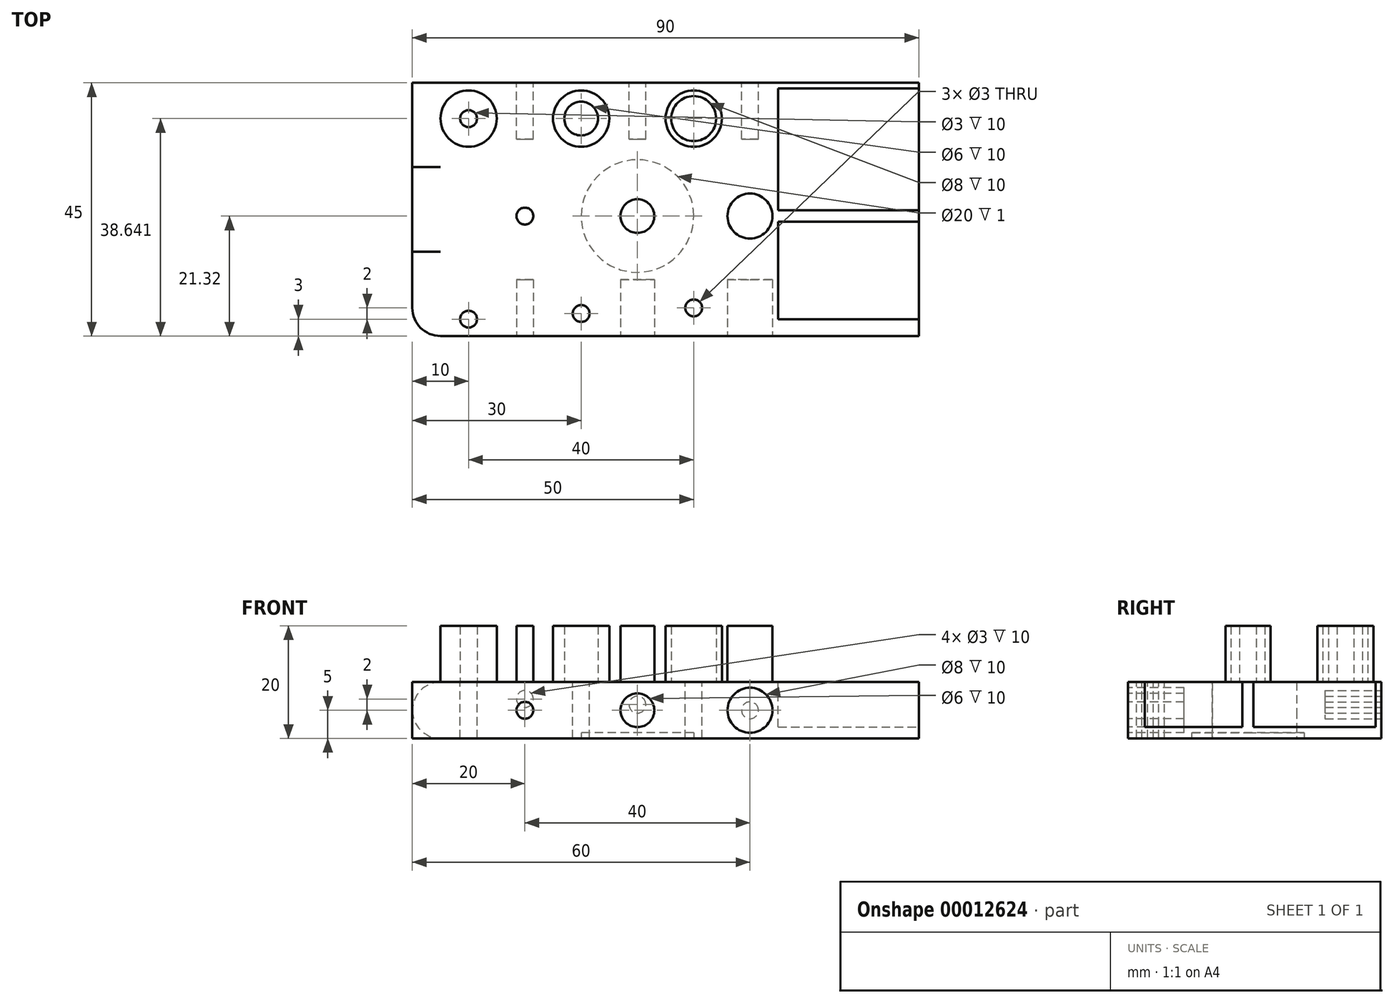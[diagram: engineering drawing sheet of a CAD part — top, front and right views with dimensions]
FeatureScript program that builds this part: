
annotation { "Feature Type Name" : "Feature", "Feature Type Description" : "" }
export const myFeature = defineFeature(function(context is Context, id is Id, definition is map)
    precondition{}
    {
        {
            var Q0;
            Q0=qCreatedBy(makeId("Top.planeOp"),FACE);
            var sketch = newSketch(context, id + "F0", { "sketchPlane" : qUnion([Q0])});
            skCircle(sketch, "E0", {"center": v(-20, 0) * mm, "radius": 1.5 * mm});
            skCircle(sketch, "E1", {"center": v(0, 0) * mm, "radius": 3 * mm});
            skCircle(sketch, "E2", {"center": v(20, 0) * mm, "radius": 4 * mm});
            skCircle(sketch, "E3", {"center": v(-10, 17.32) * mm, "radius": 5 * mm});
            skCircle(sketch, "E4", {"center": v(-30, 17.32) * mm, "radius": 5 * mm});
            skCircle(sketch, "E5", {"center": v(10, 17.32) * mm, "radius": 5 * mm});
            skCircle(sketch, "E6", {"center": v(-30, 17.32) * mm, "radius": 1.5 * mm});
            skCircle(sketch, "E7", {"center": v(-10, 17.32) * mm, "radius": 3 * mm});
            skCircle(sketch, "E8", {"center": v(10, 17.32) * mm, "radius": 4 * mm});
            skCircle(sketch, "E9", {"center": v(-30, -18.32) * mm, "radius": 1.5 * mm});
            skCircle(sketch, "E10", {"center": v(-10, -17.32) * mm, "radius": 1.5 * mm});
            skCircle(sketch, "E11", {"center": v(10, -16.32) * mm, "radius": 1.5 * mm});
            skLineSegment(sketch, "E12.bottom", {"start": v(-40, 23.68) * mm, "end": v(25, 23.68) * mm});
            skLineSegment(sketch, "E12.top", {"start": v(-40, -21.32) * mm, "end": v(25, -21.32) * mm});
            skLineSegment(sketch, "E12.left", {"start": v(-40, 23.68) * mm, "end": v(-40, -21.32) * mm});
            skLineSegment(sketch, "E12.right", {"start": v(25, 23.68) * mm, "end": v(25, -21.32) * mm});
            skLineSegment(sketch, "E13", {"start": v(-20, 0) * mm, "end": v(0, 0) * mm, "construction": true});
            skLineSegment(sketch, "E14", {"start": v(0, 0) * mm, "end": v(20, 0) * mm, "construction": true});
            skLineSegment(sketch, "E15", {"start": v(-30, 17.32) * mm, "end": v(-10, 17.32) * mm, "construction": true});
            skLineSegment(sketch, "E16", {"start": v(-10, 17.32) * mm, "end": v(10, 17.32) * mm, "construction": true});
            skLineSegment(sketch, "E17", {"start": v(0, 0) * mm, "end": v(10, 17.32) * mm, "construction": true});
            skLineSegment(sketch, "E18", {"start": v(20, 0) * mm, "end": v(10, 17.32) * mm, "construction": true});
            skLineSegment(sketch, "E19", {"start": v(-20, 0) * mm, "end": v(-10, -17.32) * mm, "construction": true});
            skLineSegment(sketch, "E20", {"start": v(0, 0) * mm, "end": v(-10, -17.32) * mm, "construction": true});
            skLineSegment(sketch, "E21.bottom", {"start": v(25, 23.68) * mm, "end": v(50, 23.68) * mm});
            skLineSegment(sketch, "E21.top", {"start": v(25, -21.32) * mm, "end": v(50, -21.32) * mm});
            skLineSegment(sketch, "E21.right", {"start": v(50, 23.68) * mm, "end": v(50, -21.32) * mm});
            skLineSegment(sketch, "E22.top", {"start": v(25, 22.68) * mm, "end": v(50, 22.68) * mm});
            skLineSegment(sketch, "E22.left", {"start": v(25, 23.68) * mm, "end": v(25, 22.68) * mm});
            skLineSegment(sketch, "E22.right", {"start": v(50, 23.68) * mm, "end": v(50, 22.68) * mm});
            skLineSegment(sketch, "E23.bottom", {"start": v(25, 1) * mm, "end": v(50, 1) * mm});
            skLineSegment(sketch, "E23.top", {"start": v(25, -1) * mm, "end": v(50, -1) * mm});
            skLineSegment(sketch, "E23.left", {"start": v(25, 1) * mm, "end": v(25, -1) * mm});
            skLineSegment(sketch, "E23.right", {"start": v(50, 1) * mm, "end": v(50, -1) * mm});
            skLineSegment(sketch, "E24.top", {"start": v(25, -18.32) * mm, "end": v(50, -18.32) * mm});
            skLineSegment(sketch, "E24.left", {"start": v(25, -21.32) * mm, "end": v(25, -18.32) * mm});
            skLineSegment(sketch, "E24.right", {"start": v(50, -21.32) * mm, "end": v(50, -18.32) * mm});
            skPoint(sketch, "E25", {"position": v(50, 0) * mm});
            skSolve(sketch);
        }
        {
            var Q0;
            Q0=qCreatedBy(makeId("Top.planeOp"),FACE);
            var sketch = newSketch(context, id + "F1", { "sketchPlane" : qUnion([Q0])});
            skLineSegment(sketch, "E26.0", {"start": v(-40, 23.68) * mm, "end": v(25, 23.68) * mm});
            skLineSegment(sketch, "E26.1", {"start": v(25, 23.68) * mm, "end": v(50, 23.68) * mm});
            skLineSegment(sketch, "E26.2", {"start": v(50, 23.68) * mm, "end": v(50, -21.32) * mm});
            skLineSegment(sketch, "E26.3", {"start": v(25, -21.32) * mm, "end": v(50, -21.32) * mm});
            skLineSegment(sketch, "E26.4", {"start": v(-40, -21.32) * mm, "end": v(25, -21.32) * mm});
            skLineSegment(sketch, "E26.5", {"start": v(-40, 23.68) * mm, "end": v(-40, -21.32) * mm});
            skSolve(sketch);
        }
        {
            var Q0;
            Q0 = qSketchRegion(id + "F1", true);
            extrude(context, id + "F2", {"entities" : qUnion([Q0]), "depth" : 10 * mm});
        }
        {
            var Q0;
            Q0=makeQuery(id+"F2.opExtrude","CAP_FACE",FACE,{"disambiguationData":[OSD([sQuery(id+"F1.wireOp",EDGE,"E26.0"),sQuery(id+"F1.wireOp",EDGE,"E26.1"),sQuery(id+"F1.wireOp",EDGE,"E26.2"),sQuery(id+"F1.wireOp",EDGE,"E26.3"),sQuery(id+"F1.wireOp",EDGE,"E26.4"),sQuery(id+"F1.wireOp",EDGE,"E26.5")])],"isStart":false});
            var sketch = newSketch(context, id + "F3", { "sketchPlane" : qUnion([Q0])});
            skCircle(sketch, "E27.0", {"center": v(-30, 17.32) * mm, "radius": 1.5 * mm});
            skCircle(sketch, "E27.1", {"center": v(-30, 17.32) * mm, "radius": 5 * mm});
            skCircle(sketch, "E27.2", {"center": v(-10, 17.32) * mm, "radius": 3 * mm});
            skCircle(sketch, "E27.3", {"center": v(-10, 17.32) * mm, "radius": 5 * mm});
            skCircle(sketch, "E27.4", {"center": v(10, 17.32) * mm, "radius": 4 * mm});
            skCircle(sketch, "E27.5", {"center": v(10, 17.32) * mm, "radius": 5 * mm});
            skCircle(sketch, "E27.6", {"center": v(20, 0) * mm, "radius": 4 * mm});
            skCircle(sketch, "E27.7", {"center": v(0, 0) * mm, "radius": 3 * mm});
            skCircle(sketch, "E27.8", {"center": v(-20, 0) * mm, "radius": 1.5 * mm});
            skSolve(sketch);
        }
        {
            var Q0;
            Q0 = qSketchRegion(id + "F3", true);
            extrude(context, id + "F4", {"entities" : qUnion([Q0]), "operationType" : NewBodyOperationType.ADD, "depth" : 10 * mm});
        }
        {
            var Q0;
            {var subQ0=sQuery(id+"F1.wireOp",EDGE,"E26.0");var subQ1=sQuery(id+"F1.wireOp",EDGE,"E26.1");var subQ2=sQuery(id+"F1.wireOp",EDGE,"E26.2");var subQ3=sQuery(id+"F1.wireOp",EDGE,"E26.3");var subQ4=sQuery(id+"F1.wireOp",EDGE,"E26.4");var subQ5=sQuery(id+"F1.wireOp",EDGE,"E26.5");Q0=makeQuery(id+"F4.boolean.opBoolean","SPLIT",FACE,{"disambiguationData":[TD([makeQuery(id+"F2.opExtrude","SWEPT_FACE",FACE,{"disambiguationData":[OSD([subQ2])]})])],"derivedFrom":makeQuery(id+"F2.opExtrude","CAP_FACE",FACE,{"disambiguationData":[OSD([subQ0,subQ1,subQ2,subQ3,subQ4,subQ5])],"isStart":false})});}
            var sketch = newSketch(context, id + "F5", { "sketchPlane" : qUnion([Q0])});
            skCircle(sketch, "E28.0", {"center": v(-30, -18.32) * mm, "radius": 1.5 * mm});
            skCircle(sketch, "E28.1", {"center": v(-10, -17.32) * mm, "radius": 1.5 * mm});
            skCircle(sketch, "E28.2", {"center": v(10, -16.32) * mm, "radius": 1.5 * mm});
            skSolve(sketch);
        }
        {
            var Q0;
            Q0 = qSketchRegion(id + "F5", true);
            extrude(context, id + "F6", {"entities" : qUnion([Q0]), "operationType" : NewBodyOperationType.REMOVE, "endBound" : BoundingType.THROUGH_ALL, "oppositeDirection" : true, "depth" : 25 * mm});
        }
        {
            var Q0;
            {var subQ0=sQuery(id+"F1.wireOp",EDGE,"E26.0");var subQ1=sQuery(id+"F1.wireOp",EDGE,"E26.1");var subQ2=sQuery(id+"F1.wireOp",EDGE,"E26.2");var subQ3=sQuery(id+"F1.wireOp",EDGE,"E26.3");var subQ4=sQuery(id+"F1.wireOp",EDGE,"E26.4");var subQ5=sQuery(id+"F1.wireOp",EDGE,"E26.5");Q0=makeQuery(id+"F4.boolean.opBoolean","SPLIT",FACE,{"disambiguationData":[TD([makeQuery(id+"F2.opExtrude","SWEPT_FACE",FACE,{"disambiguationData":[OSD([subQ2])]})])],"derivedFrom":makeQuery(id+"F2.opExtrude","CAP_FACE",FACE,{"disambiguationData":[OSD([subQ0,subQ1,subQ2,subQ3,subQ4,subQ5])],"isStart":false})});}
            var sketch = newSketch(context, id + "F7", { "sketchPlane" : qUnion([Q0])});
            skLineSegment(sketch, "E29.bottom", {"start": v(25, 22.68) * mm, "end": v(50, 22.68) * mm});
            skLineSegment(sketch, "E29.top", {"start": v(25, 1) * mm, "end": v(50, 1) * mm});
            skLineSegment(sketch, "E29.left", {"start": v(25, 22.68) * mm, "end": v(25, 1) * mm});
            skLineSegment(sketch, "E29.right", {"start": v(50, 22.68) * mm, "end": v(50, 1) * mm});
            skLineSegment(sketch, "E30.bottom", {"start": v(25, -1) * mm, "end": v(50, -1) * mm});
            skLineSegment(sketch, "E30.top", {"start": v(25, -18.32) * mm, "end": v(50, -18.32) * mm});
            skLineSegment(sketch, "E30.left", {"start": v(25, -1) * mm, "end": v(25, -18.32) * mm});
            skLineSegment(sketch, "E30.right", {"start": v(50, -1) * mm, "end": v(50, -18.32) * mm});
            skSolve(sketch);
        }
        {
            var Q0;
            Q0 = qSketchRegion(id + "F7", true);
            extrude(context, id + "F8", {"entities" : qUnion([Q0]), "operationType" : NewBodyOperationType.REMOVE, "oppositeDirection" : true, "depth" : 8 * mm});
        }
        {
            var Q0;
            Q0=makeQuery(id+"F2.opExtrude","SWEPT_FACE",FACE,{"disambiguationData":[OSD([sQuery(id+"F1.wireOp",EDGE,"E26.3"),sQuery(id+"F1.wireOp",EDGE,"E26.4")])]});
            var sketch = newSketch(context, id + "F9", { "sketchPlane" : qUnion([Q0])});
            skCircle(sketch, "E31", {"center": v(-20, 5) * mm, "radius": 1.5 * mm});
            skCircle(sketch, "E32", {"center": v(0, 5) * mm, "radius": 3 * mm});
            skCircle(sketch, "E33", {"center": v(20, 5) * mm, "radius": 4 * mm});
            skSolve(sketch);
        }
        {
            var Q0;
            Q0 = qSketchRegion(id + "F9", true);
            extrude(context, id + "F10", {"entities" : qUnion([Q0]), "operationType" : NewBodyOperationType.REMOVE, "oppositeDirection" : true, "depth" : 10 * mm});
        }
        {
            var Q0;
            Q0=makeQuery(id+"F2.opExtrude","SWEPT_FACE",FACE,{"disambiguationData":[OSD([sQuery(id+"F1.wireOp",EDGE,"E26.0"),sQuery(id+"F1.wireOp",EDGE,"E26.1")])]});
            var sketch = newSketch(context, id + "F11", { "sketchPlane" : qUnion([Q0])});
            skCircle(sketch, "E34", {"center": v(-20, 5) * mm, "radius": 1.5 * mm});
            skCircle(sketch, "E35", {"center": v(0, 6) * mm, "radius": 1.5 * mm});
            skCircle(sketch, "E36", {"center": v(20, 7) * mm, "radius": 1.5 * mm});
            skPoint(sketch, "E37", {"position": v(0, 0) * mm});
            skSolve(sketch);
        }
        {
            var Q0;
            Q0 = qSketchRegion(id + "F11", true);
            extrude(context, id + "F12", {"entities" : qUnion([Q0]), "operationType" : NewBodyOperationType.REMOVE, "oppositeDirection" : true, "depth" : 10 * mm});
        }
        {
            var Q0;
            Q0=makeQuery(id+"F2.opExtrude","SWEPT_EDGE",EDGE,{"disambiguationData":[OSD([sQuery(id+"F1.wireOp",EDGE,"E26.4"),sQuery(id+"F1.wireOp",EDGE,"E26.5")])]});
            fillet(context, id + "F13", {"entities" : qUnion([Q0]), "radius" : 5 * mm, "tangentPropagation" : true, "allowEdgeOverflow" : false});
        }
        {
            var Q0;
            Q0=makeQuery(id+"F2.opExtrude","SWEPT_FACE",FACE,{"disambiguationData":[OSD([sQuery(id+"F1.wireOp",EDGE,"E26.5")])]});
            var sketch = newSketch(context, id + "F14", { "sketchPlane" : qUnion([Q0])});
            skLineSegment(sketch, "E38.bottom", {"start": v(-8.68, 10) * mm, "end": v(6.32, 10) * mm});
            skLineSegment(sketch, "E38.top", {"start": v(-8.68, 0) * mm, "end": v(6.32, 0) * mm});
            skLineSegment(sketch, "E38.left", {"start": v(-8.68, 10) * mm, "end": v(-8.68, 0) * mm});
            skLineSegment(sketch, "E38.right", {"start": v(6.32, 10) * mm, "end": v(6.32, 0) * mm});
            skSolve(sketch);
        }
        {
            var Q0;
            Q0 = qSketchRegion(id + "F14", true);
            extrude(context, id + "F15", {"entities" : qUnion([Q0]), "operationType" : NewBodyOperationType.REMOVE, "oppositeDirection" : true, "depth" : 5 * mm});
        }
        {
            var Q0;
            Q0=makeQuery(id+"F15.boolean.opBoolean","COPY",FACE,{"derivedFrom":makeQuery(id+"F15.opExtrude","SWEPT_FACE",FACE,{"disambiguationData":[OSD([sQuery(id+"F14.wireOp",EDGE,"E38.left")])]})});
            var sketch = newSketch(context, id + "F16", { "sketchPlane" : qUnion([Q0])});
            skArc(sketch, "E39", {"start": v(-35, 10) * mm, "mid": v(-40, 5) * mm, "end": v(-35, 0) * mm});
            skLineSegment(sketch, "E40", {"start": v(-35, 10) * mm, "end": v(-35, 0) * mm});
            skSolve(sketch);
        }
        {
            var Q0;
            Q0 = qSketchRegion(id + "F16", true);
            extrude(context, id + "F17", {"entities" : qUnion([Q0]), "operationType" : NewBodyOperationType.ADD, "endBound" : BoundingType.UP_TO_NEXT, "depth" : 25 * mm});
        }
        {
            var Q0;
            Q0=makeQuery(id+"F0.imprint","IMPRINT",FACE,{"disambiguationData":[TD([[makeQuery(id+"F0.imprint","IMPRINT",EDGE,{"derivedFrom":sQuery(id+"F0.wireOp",EDGE,"E0")}),-1.0]])]});
            var sketch = newSketch(context, id + "F18", { "sketchPlane" : qUnion([Q0])});
            skCircle(sketch, "E41", {"center": v(0, 0) * mm, "radius": 10 * mm});
            skSolve(sketch);
        }
        {
            var Q0;
            Q0 = qSketchRegion(id + "F18", true);
            extrude(context, id + "F19", {"entities" : qUnion([Q0]), "operationType" : NewBodyOperationType.REMOVE, "depth" : 1 * mm});
        }
    });
